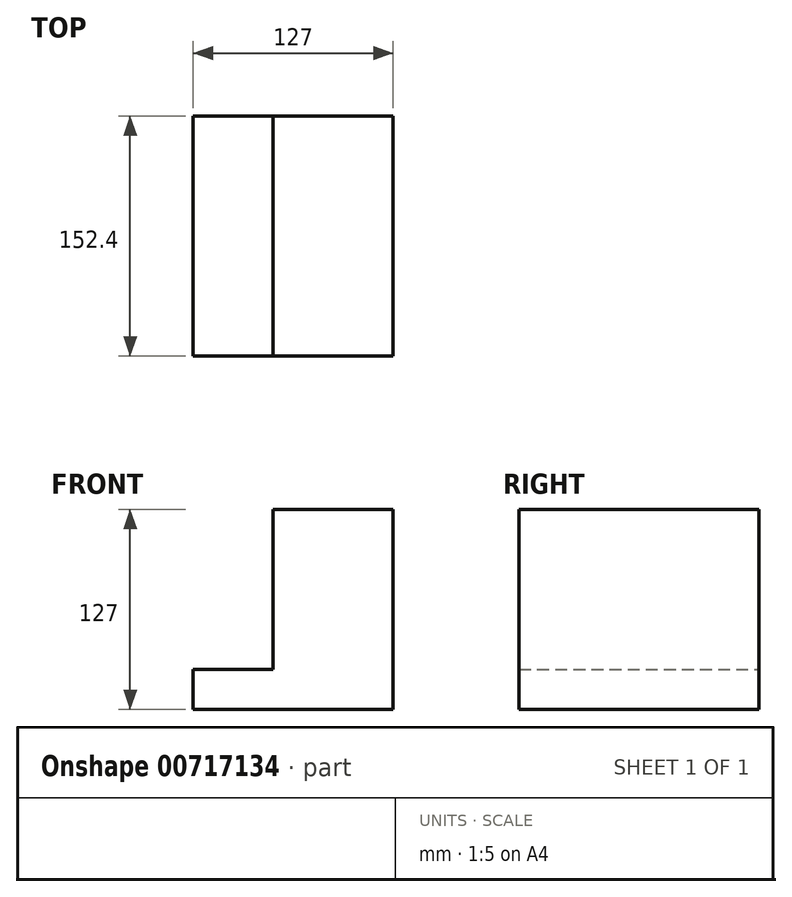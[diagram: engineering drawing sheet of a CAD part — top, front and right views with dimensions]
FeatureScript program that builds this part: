
annotation { "Feature Type Name" : "Feature", "Feature Type Description" : "" }
export const myFeature = defineFeature(function(context is Context, id is Id, definition is map)
    precondition{}
    {
        {
            var Q0;
            Q0=qCreatedBy(makeId("Front.planeOp"),FACE);
            var sketch = newSketch(context, id + "F0", { "sketchPlane" : qUnion([Q0])});
            skLineSegment(sketch, "E0", {"start": v(-127.75, -59.72) * mm, "end": v(-0.75, -59.72) * mm});
            skLineSegment(sketch, "E1", {"start": v(-0.75, -59.72) * mm, "end": v(-0.75, 67.28) * mm});
            skLineSegment(sketch, "E2", {"start": v(-0.75, 67.28) * mm, "end": v(-76.95, 67.28) * mm});
            skLineSegment(sketch, "E3", {"start": v(-76.95, 67.28) * mm, "end": v(-76.95, -34.32) * mm});
            skLineSegment(sketch, "E4", {"start": v(-76.95, -34.32) * mm, "end": v(-127.75, -34.32) * mm});
            skLineSegment(sketch, "E5", {"start": v(-127.75, -34.32) * mm, "end": v(-127.75, -59.72) * mm});
            skSolve(sketch);
        }
        {
            var Q0;
            Q0=makeQuery(id+"F0.imprint","IMPRINT",FACE,{"disambiguationData":[TD([[makeQuery(id+"F0.imprint","IMPRINT",EDGE,{"derivedFrom":sQuery(id+"F0.wireOp",EDGE,"E0")}),1.0]])]});
            extrude(context, id + "F1", {"entities" : qUnion([Q0]), "depth" : 152.4 * mm, "offsetDistance" : 25.4 * mm});
        }
    });
